# Revit family: E 0300 LUM
name_source: partatom
category: Lighting Fixtures
revit_build: Autodesk Revit 2017 (Build: 20160225_1515(x64)
units: mm (PartAtom-declared; Revit-internal decimal feet)

## family parameters
Cut with Voids When Loaded = No
Host = Face
Light Source = Yes
Part Type = Normal
Room Calculation Point = No
Round Connector Dimension = Use Diameter
Shared = No

## types (1)
- ELUM.0300.10.40
    Apparent Load = 10 VA
    Color Filter = 16777215
    Default Elevation = 1219 mm
    Dimming Lamp Color Temperature Shift = <None>
    Emit Shape Visible in Rendering = Yes
    Emit from Rectangle Length = 284 mm  [stored 0.931759 ft]
    Emit from Rectangle Width = 54 mm  [stored 0.177165 ft]
    Lamp = LED
    Manufacturer = ARLIGHT AYDINLATMA A.Ş.
    Model = E0300LUM
    Photometric Web File = e-0300-lum-10w-4k-80ra-rg-035.ies
    Tilt Angle = 90.00°
    Type Comments = Industrial Lighting
    URL = arlight.net/en/products/indoor/industrial-lighting-fixtures/lumo
    Wattage Comments = 10W

note: [stored X ft] marks values corroborated as IEEE doubles in the binary element streams (Revit-internal decimal feet)

## geometry (parser evidence)
native form markers: Blend x2, Sweep x3
no freeform markers — native parametric forms only
